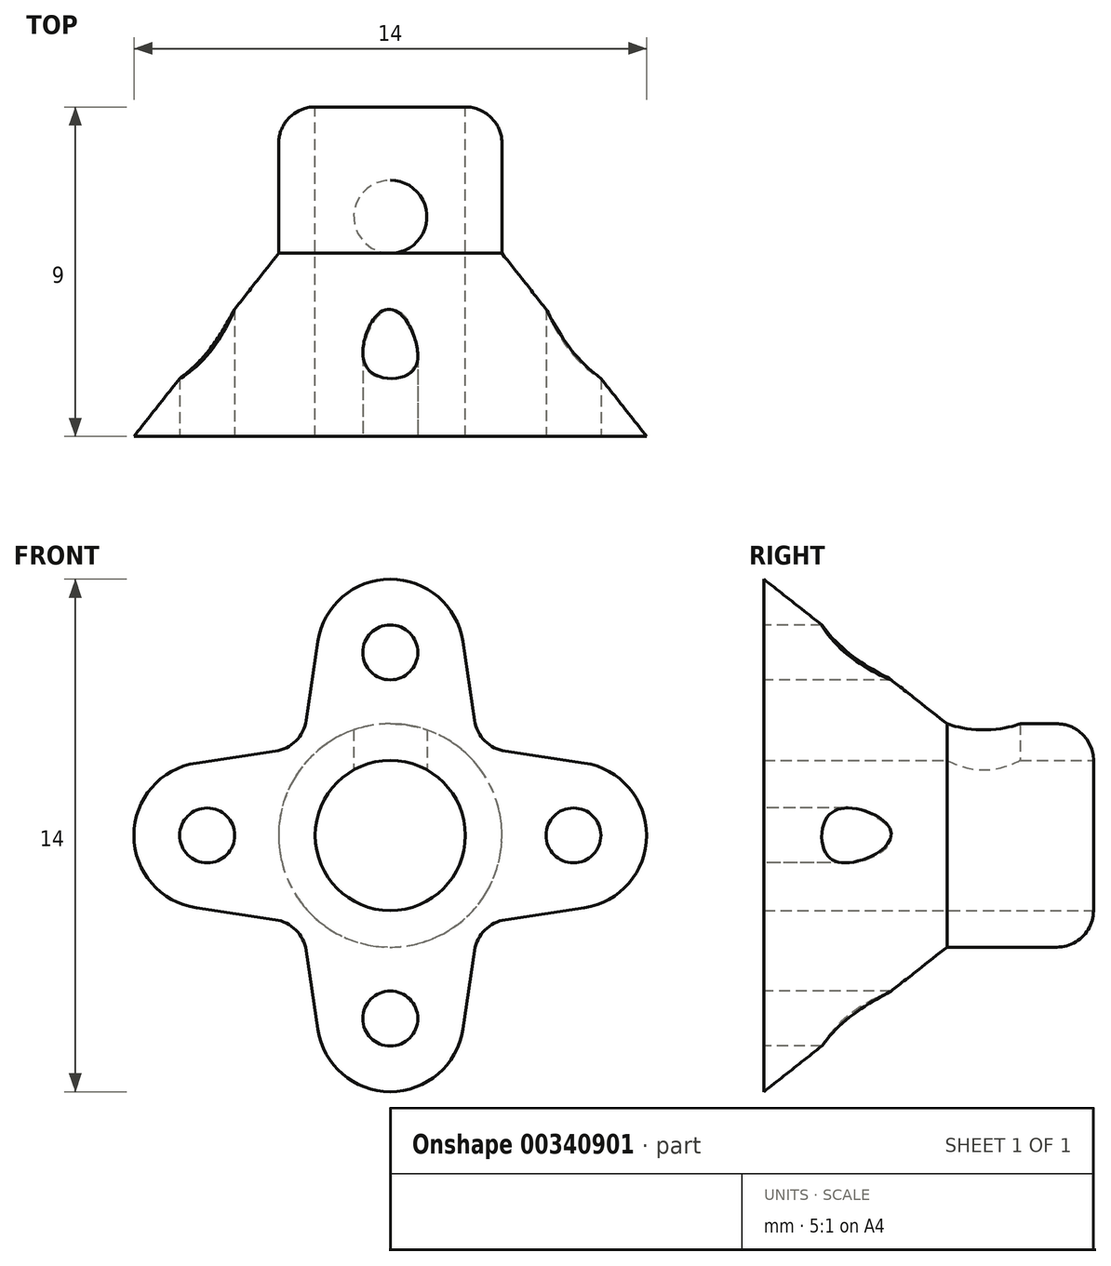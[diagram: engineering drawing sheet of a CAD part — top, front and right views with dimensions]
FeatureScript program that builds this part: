
annotation { "Feature Type Name" : "Feature", "Feature Type Description" : "" }
export const myFeature = defineFeature(function(context is Context, id is Id, definition is map)
    precondition{}
    {
        {
            var Q0;
            Q0=qCreatedBy(makeId("Front.planeOp"),FACE);
            var sketch = newSketch(context, id + "F0", { "sketchPlane" : qUnion([Q0])});
            skCircle(sketch, "E0", {"center": v(0, 0) * mm, "radius": 2.05 * mm});
            skCircle(sketch, "E1", {"center": v(0, 0) * mm, "radius": 3.05 * mm});
            skSolve(sketch);
        }
        {
            var Q0;
            Q0 = qSketchRegion(id + "F0", true);
            var Q1;
            Q1=makeQuery(id+"F0.imprint","IMPRINT",FACE,{"disambiguationData":[TD([[makeQuery(id+"F0.imprint","IMPRINT",EDGE,{"derivedFrom":sQuery(id+"F0.wireOp",EDGE,"E0")}),1.0]])]});
            extrude(context, id + "F1", {"entities" : qUnion([Q0, Q1]), "depth" : 4 * mm, "offsetDistance" : 25 * mm});
        }
        {
            var Q0;
            Q0=makeQuery(id+"F1.opExtrude","CAP_FACE",FACE,{"disambiguationData":[OSD([sQuery(id+"F0.wireOp",EDGE,"E0"),sQuery(id+"F0.wireOp",EDGE,"E1")])],"isStart":false});
            cPlane(context, id + "F2", {"entities" : qUnion([Q0]), "cplaneType" : CPlaneType.OFFSET, "offset" : 5 * mm, "width" : 150 * mm, "height" : 150 * mm});
        }
        {
            var Q0;
            Q0=qCreatedBy(id+"F2.planeOp",FACE);
            var sketch = newSketch(context, id + "F3", { "sketchPlane" : qUnion([Q0])});
            skLineSegment(sketch, "E2", {"start": v(-2.3, 3.14) * mm, "end": v(-1.98, 5.3) * mm});
            skLineSegment(sketch, "E3", {"start": v(-3.14, 2.3) * mm, "end": v(-5.3, 1.98) * mm});
            skArc(sketch, "E4", {"start": v(-3.14, 2.3) * mm, "mid": v(-2.58, 2.58) * mm, "end": v(-2.3, 3.14) * mm});
            skArc(sketch, "E5", {"start": v(-1.98, 5.3) * mm, "mid": v(0, 7) * mm, "end": v(1.98, 5.3) * mm});
            skArc(sketch, "E6", {"start": v(-5.3, 1.98) * mm, "mid": v(-7, 0) * mm, "end": v(-5.3, -1.98) * mm});
            skLineSegment(sketch, "E7", {"start": v(-5, 0) * mm, "end": v(0, 5) * mm, "construction": true});
            skLineSegment(sketch, "E8", {"start": v(-3.29, 3.29) * mm, "end": v(0, 0) * mm, "construction": true});
            skLineSegment(sketch, "E9", {"start": v(-5.3, -1.98) * mm, "end": v(-3.14, -2.3) * mm});
            skArc(sketch, "E10", {"start": v(-3.14, -2.3) * mm, "mid": v(-2.58, -2.58) * mm, "end": v(-2.3, -3.14) * mm});
            skLineSegment(sketch, "E11", {"start": v(-2.3, -3.14) * mm, "end": v(-1.98, -5.3) * mm});
            skArc(sketch, "E12", {"start": v(-1.98, -5.3) * mm, "mid": v(0, -7) * mm, "end": v(1.98, -5.3) * mm});
            skLineSegment(sketch, "E13", {"start": v(1.98, -5.3) * mm, "end": v(2.3, -3.14) * mm});
            skArc(sketch, "E14", {"start": v(2.3, -3.14) * mm, "mid": v(2.58, -2.58) * mm, "end": v(3.14, -2.3) * mm});
            skLineSegment(sketch, "E15", {"start": v(3.14, -2.3) * mm, "end": v(5.3, -1.98) * mm});
            skArc(sketch, "E16", {"start": v(5.3, -1.98) * mm, "mid": v(7, 0) * mm, "end": v(5.3, 1.98) * mm});
            skLineSegment(sketch, "E17", {"start": v(5.3, 1.98) * mm, "end": v(3.14, 2.3) * mm});
            skLineSegment(sketch, "E18", {"start": v(1.98, 5.3) * mm, "end": v(2.3, 3.14) * mm});
            skArc(sketch, "E19", {"start": v(2.3, 3.14) * mm, "mid": v(2.58, 2.58) * mm, "end": v(3.14, 2.3) * mm});
            skCircle(sketch, "E20", {"center": v(-5, 0) * mm, "radius": 0.75 * mm, "construction": true});
            skCircle(sketch, "E21", {"center": v(0, 5) * mm, "radius": 0.75 * mm, "construction": true});
            skCircle(sketch, "E22", {"center": v(5, 0) * mm, "radius": 0.75 * mm, "construction": true});
            skCircle(sketch, "E23", {"center": v(0, -5) * mm, "radius": 0.75 * mm, "construction": true});
            skSolve(sketch);
        }
        {
            var Q1;
            Q1=makeQuery(id+"F3.imprint","IMPRINT",FACE,{"disambiguationData":[TD([[makeQuery(id+"F3.imprint","IMPRINT",EDGE,{"derivedFrom":sQuery(id+"F3.wireOp",EDGE,"E2")}),-1.0]])]});
            var Q2;
            Q2=makeQuery(id+"F1.opExtrude","CAP_FACE",FACE,{"disambiguationData":[OSD([sQuery(id+"F0.wireOp",EDGE,"E1")])],"isStart":false});
            loft(context, id + "F4", {"operationType" : NewBodyOperationType.ADD, "sheetProfilesArray" : [{ "sheetProfileEntities" : qUnion([Q1]) }, { "sheetProfileEntities" : qUnion([Q2]) }]});
        }
        {
            var Q0;
            Q0=sQuery(id+"F3.wireOp",VERTEX,"E16.center");
            var Q1;
            Q1=sQuery(id+"F3.wireOp",VERTEX,"E12.center");
            var Q2;
            Q2=sQuery(id+"F3.wireOp",VERTEX,"E7.start");
            var Q3;
            Q3=sQuery(id+"F3.wireOp",VERTEX,"E7.end");
            var Q4;
            Q4=makeQuery(id+"F1.opExtrude","SWEPT_BODY",BODY,{"disambiguationData":[OSD([sQuery(id+"F0.wireOp",EDGE,"E1")])]});
            hole(context, id + "F5", {"style" : HoleStyle.SIMPLE, "endStyle" : HoleEndStyle.THROUGH, "holeDiameter" : 1.5 * mm, "majorDiameter" : 5 * mm, "isTappedThrough" : true, "tappedDepth" : 12 * mm, "tapClearance" : 3, "locations" : qUnion([Q0, Q1, Q2, Q3]), "scope" : qUnion([Q4])});
        }
        {
            var Q0;
            Q0=makeQuery(id+"F0.imprint","IMPRINT",FACE,{"disambiguationData":[TD([[makeQuery(id+"F0.imprint","IMPRINT",EDGE,{"derivedFrom":sQuery(id+"F0.wireOp",EDGE,"E0")}),1.0]])]});
            extrude(context, id + "F6", {"entities" : qUnion([Q0]), "operationType" : NewBodyOperationType.REMOVE, "depth" : 25 * mm, "offsetDistance" : 25 * mm});
        }
        {
            var Q0;
            Q0=qCreatedBy(makeId("Top.planeOp"),FACE);
            var sketch = newSketch(context, id + "F7", { "sketchPlane" : qUnion([Q0])});
            skPoint(sketch, "E24", {"position": v(0, -3) * mm});
            skSolve(sketch);
        }
        {
            var Q0;
            Q0=sQuery(id+"F7.wireOp",VERTEX,"E24");
            var Q1;
            Q1=makeQuery(id+"F1.opExtrude","SWEPT_BODY",BODY,{"disambiguationData":[OSD([sQuery(id+"F0.wireOp",EDGE,"E1")])]});
            hole(context, id + "F8", {"style" : HoleStyle.SIMPLE, "endStyle" : HoleEndStyle.THROUGH, "oppositeDirection" : true, "holeDiameter" : 2 * mm, "majorDiameter" : 5 * mm, "isTappedThrough" : true, "tappedDepth" : 12 * mm, "tapClearance" : 3, "locations" : qUnion([Q0]), "scope" : qUnion([Q1])});
        }
        {
            var Q0;
            Q0=makeQuery(id+"F1.opExtrude","CAP_EDGE",EDGE,{"disambiguationData":[OSD([sQuery(id+"F0.wireOp",EDGE,"E1")])],"isStart":true});
            fillet(context, id + "F9", {"entities" : qUnion([Q0]), "radius" : 1 * mm, "tangentPropagation" : true, "allowEdgeOverflow" : false});
        }
    });
